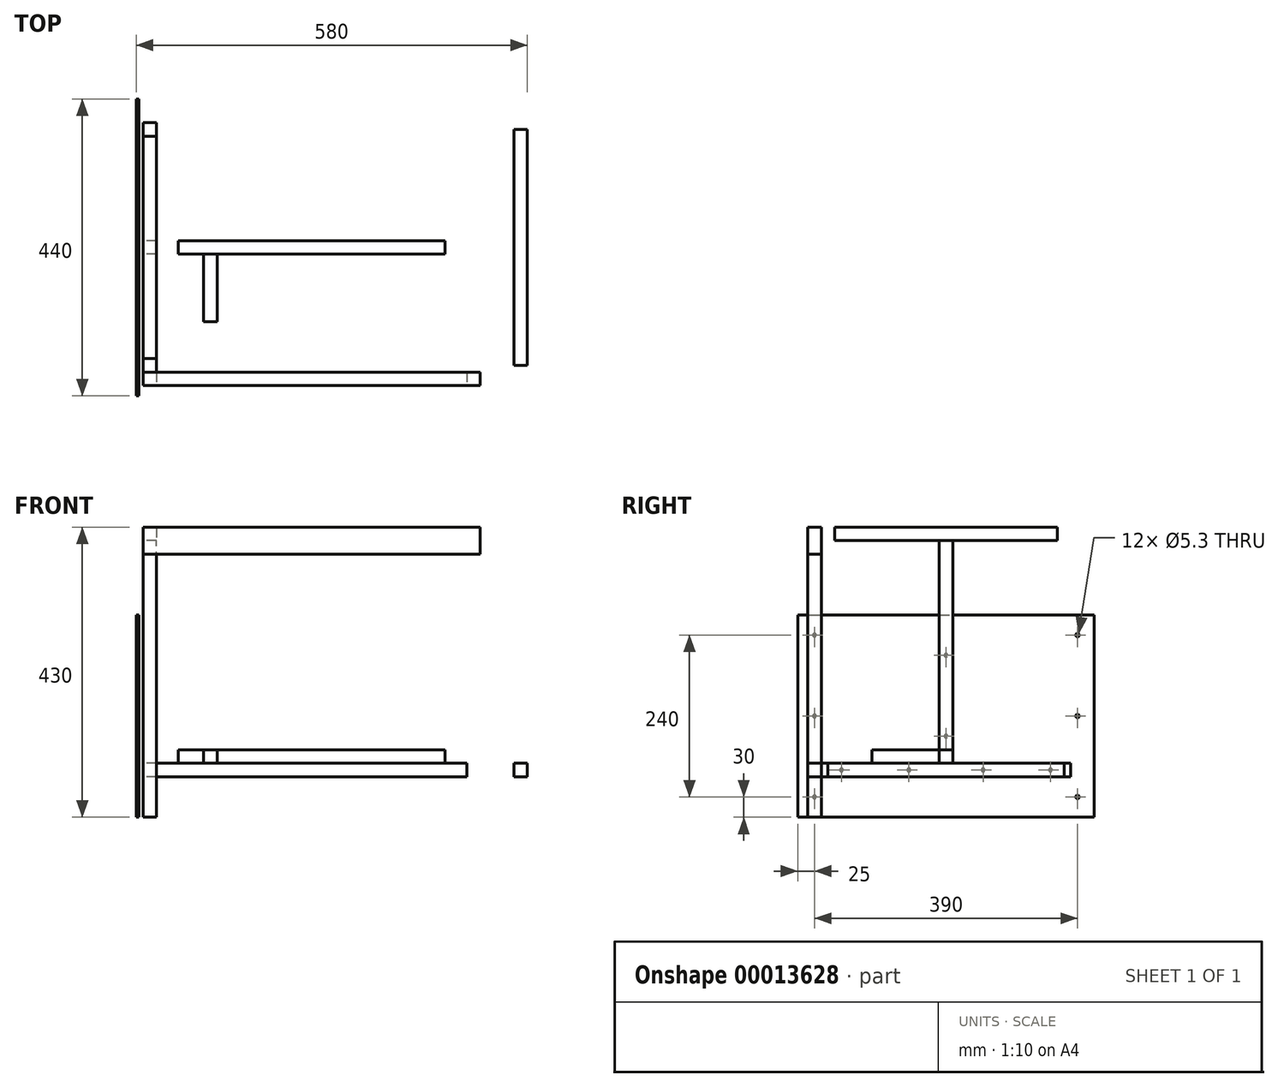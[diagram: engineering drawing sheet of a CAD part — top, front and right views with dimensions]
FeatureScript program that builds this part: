
annotation { "Feature Type Name" : "Feature", "Feature Type Description" : "" }
export const myFeature = defineFeature(function(context is Context, id is Id, definition is map)
    precondition{}
    {
        {
            var Q0;
            Q0=qCreatedBy(makeId("Top.planeOp"),FACE);
            var sketch = newSketch(context, id + "F0", { "sketchPlane" : qUnion([Q0])});
            skLineSegment(sketch, "E0.rect.bottom", {"start": v(230, 185) * mm, "end": v(-230, 185) * mm});
            skLineSegment(sketch, "E0.rect.top", {"start": v(230, -185) * mm, "end": v(-230, -185) * mm});
            skLineSegment(sketch, "E0.rect.left", {"start": v(230, 185) * mm, "end": v(230, -185) * mm});
            skLineSegment(sketch, "E0.rect.right", {"start": v(-230, 185) * mm, "end": v(-230, -185) * mm});
            skPoint(sketch, "E0.rect.middle", {"position": v(0, 0) * mm});
            skLineSegment(sketch, "E1.0", {"start": v(-250, 205) * mm, "end": v(-250, -205) * mm});
            skLineSegment(sketch, "E1.1", {"start": v(250, 205) * mm, "end": v(-250, 205) * mm});
            skLineSegment(sketch, "E1.2", {"start": v(250, 205) * mm, "end": v(250, -205) * mm});
            skLineSegment(sketch, "E1.3", {"start": v(250, -205) * mm, "end": v(-250, -205) * mm});
            skLineSegment(sketch, "E2", {"start": v(230, -185) * mm, "end": v(250, -185) * mm});
            skLineSegment(sketch, "E3", {"start": v(230, -185) * mm, "end": v(230, -205) * mm});
            skLineSegment(sketch, "E4", {"start": v(-230, -185) * mm, "end": v(-230, -205) * mm});
            skLineSegment(sketch, "E5", {"start": v(-230, -185) * mm, "end": v(-250, -185) * mm});
            skLineSegment(sketch, "E6", {"start": v(-230, 185) * mm, "end": v(-250, 185) * mm});
            skLineSegment(sketch, "E7", {"start": v(-230, 185) * mm, "end": v(-230, 205) * mm});
            skLineSegment(sketch, "E8", {"start": v(230, 185) * mm, "end": v(230, 205) * mm});
            skLineSegment(sketch, "E9", {"start": v(230, 185) * mm, "end": v(250, 185) * mm});
            skLineSegment(sketch, "E10.rect.bottom", {"start": v(198, 10) * mm, "end": v(-198, 10) * mm});
            skLineSegment(sketch, "E10.rect.top", {"start": v(198, -10) * mm, "end": v(-198, -10) * mm});
            skLineSegment(sketch, "E10.rect.left", {"start": v(198, 10) * mm, "end": v(198, -10) * mm});
            skLineSegment(sketch, "E10.rect.right", {"start": v(-198, 10) * mm, "end": v(-198, -10) * mm});
            skLineSegment(sketch, "E11", {"start": v(-160, 10) * mm, "end": v(-160, 110) * mm});
            skLineSegment(sketch, "E12", {"start": v(-160, 110) * mm, "end": v(-140, 110) * mm});
            skLineSegment(sketch, "E13", {"start": v(-140, 110) * mm, "end": v(-140, 10) * mm});
            skLineSegment(sketch, "E14", {"start": v(-140, -10) * mm, "end": v(-140, -110) * mm});
            skLineSegment(sketch, "E15", {"start": v(-140, -110) * mm, "end": v(-160, -110) * mm});
            skLineSegment(sketch, "E16", {"start": v(-160, -110) * mm, "end": v(-160, -10) * mm});
            skLineSegment(sketch, "E17", {"start": v(160, 10) * mm, "end": v(160, 110) * mm});
            skLineSegment(sketch, "E18", {"start": v(160, 110) * mm, "end": v(140, 110) * mm});
            skLineSegment(sketch, "E19", {"start": v(140, 110) * mm, "end": v(140, 10) * mm});
            skLineSegment(sketch, "E20", {"start": v(140, -10) * mm, "end": v(140, -110) * mm});
            skLineSegment(sketch, "E21", {"start": v(140, -110) * mm, "end": v(160, -110) * mm});
            skLineSegment(sketch, "E22", {"start": v(160, -110) * mm, "end": v(160, -10) * mm});
            skLineSegment(sketch, "E23", {"start": v(0, 0) * mm, "end": v(140, 0) * mm, "construction": true});
            skLineSegment(sketch, "E24", {"start": v(0, 0) * mm, "end": v(-140, 0) * mm, "construction": true});
            skLineSegment(sketch, "E25.rect.bottom", {"start": v(-184, 1) * mm, "end": v(-226, 1) * mm, "construction": true});
            skLineSegment(sketch, "E25.rect.top", {"start": v(-184, -41) * mm, "end": v(-226, -41) * mm, "construction": true});
            skLineSegment(sketch, "E25.rect.left", {"start": v(-184, 1) * mm, "end": v(-184, -41) * mm, "construction": true});
            skLineSegment(sketch, "E25.rect.right", {"start": v(-226, 1) * mm, "end": v(-226, -41) * mm, "construction": true});
            skPoint(sketch, "E25.rect.middle", {"position": v(-205, -20) * mm});
            skCircle(sketch, "E26", {"center": v(-205, -20) * mm, "radius": 12.5 * mm, "construction": true});
            skLineSegment(sketch, "E27", {"start": v(0, 0) * mm, "end": v(0, 205) * mm, "construction": true});
            skCircle(sketch, "E28.0.MirrorC", {"center": v(205, -20) * mm, "radius": 12.5 * mm, "construction": true});
            skLineSegment(sketch, "E29.0.MirrorCS", {"start": v(184, 1) * mm, "end": v(184, -41) * mm, "construction": true});
            skLineSegment(sketch, "E30.0.MirrorCS", {"start": v(184, 1) * mm, "end": v(226, 1) * mm, "construction": true});
            skLineSegment(sketch, "E31.0.MirrorCS", {"start": v(226, 1) * mm, "end": v(226, -41) * mm, "construction": true});
            skLineSegment(sketch, "E32.0.MirrorCS", {"start": v(184, -41) * mm, "end": v(226, -41) * mm, "construction": true});
            skLineSegment(sketch, "E33", {"start": v(-230, -10) * mm, "end": v(-250, -10) * mm});
            skLineSegment(sketch, "E34", {"start": v(-230, 10) * mm, "end": v(-250, 10) * mm});
            skLineSegment(sketch, "E35", {"start": v(230, 10) * mm, "end": v(250, 10) * mm});
            skLineSegment(sketch, "E36", {"start": v(230, -10) * mm, "end": v(250, -10) * mm});
            skLineSegment(sketch, "E37.rect.bottom", {"start": v(320, 175) * mm, "end": v(300, 175) * mm});
            skLineSegment(sketch, "E37.rect.top", {"start": v(320, -175) * mm, "end": v(300, -175) * mm});
            skLineSegment(sketch, "E37.rect.left", {"start": v(320, 175) * mm, "end": v(320, -175) * mm});
            skLineSegment(sketch, "E37.rect.right", {"start": v(300, 175) * mm, "end": v(300, -175) * mm});
            skPoint(sketch, "E37.rect.middle", {"position": v(310, 0) * mm});
            skCircle(sketch, "E38", {"center": v(-205, -20) * mm, "radius": 5.5 * mm, "construction": true});
            skSolve(sketch);
        }
        {
            var Q0;
            Q0=sQuery(id+"F0.wireOp",EDGE,"E1.3");
            cPlane(context, id + "F1", {"entities" : qUnion([Q0]), "cplaneType" : CPlaneType.LINE_ANGLE, "offset" : 150 * mm, "angle" : 0 * degree, "width" : 150 * mm, "height" : 150 * mm});
        }
        {
            var Q0;
            Q0=qCreatedBy(id+"F1.planeOp",FACE);
            var sketch = newSketch(context, id + "F2", { "sketchPlane" : qUnion([Q0])});
            skLineSegment(sketch, "E39.0", {"start": v(250, 0) * mm, "end": v(-230, 0) * mm});
            skLineSegment(sketch, "E40", {"start": v(-250, 0) * mm, "end": v(-250, 310) * mm});
            skLineSegment(sketch, "E41", {"start": v(-250, 310) * mm, "end": v(250, 310) * mm});
            skLineSegment(sketch, "E42", {"start": v(250, 310) * mm, "end": v(250, 0) * mm});
            skLineSegment(sketch, "E43", {"start": v(-250, 310) * mm, "end": v(-250, 350) * mm});
            skLineSegment(sketch, "E44", {"start": v(-250, 350) * mm, "end": v(250, 350) * mm});
            skLineSegment(sketch, "E45", {"start": v(250, 350) * mm, "end": v(250, 310) * mm});
            skLineSegment(sketch, "E46", {"start": v(-250, 0) * mm, "end": v(-250, -20) * mm});
            skLineSegment(sketch, "E47", {"start": v(-250, -20) * mm, "end": v(250, -20) * mm});
            skLineSegment(sketch, "E48", {"start": v(250, -20) * mm, "end": v(250, 0) * mm});
            skPoint(sketch, "E49.0", {"position": v(-230, 0) * mm});
            skPoint(sketch, "E50.0", {"position": v(230, 0) * mm});
            skLineSegment(sketch, "E51", {"start": v(230, 0) * mm, "end": v(230, -20) * mm});
            skLineSegment(sketch, "E52", {"start": v(-230, 0) * mm, "end": v(-230, -20) * mm});
            skLineSegment(sketch, "E53", {"start": v(-230, 0) * mm, "end": v(-230, 310) * mm});
            skLineSegment(sketch, "E54", {"start": v(230, 0) * mm, "end": v(230, 310) * mm});
            skLineSegment(sketch, "E55", {"start": v(-230, -20) * mm, "end": v(-230, -80) * mm});
            skLineSegment(sketch, "E56", {"start": v(-230, -80) * mm, "end": v(-250, -80) * mm});
            skLineSegment(sketch, "E57", {"start": v(-250, -80) * mm, "end": v(-250, -20) * mm});
            skSolve(sketch);
        }
        {
            var Q0;
            Q0=sQuery(id+"F0.wireOp",EDGE,"E1.0");
            cPlane(context, id + "F3", {"entities" : qUnion([Q0]), "cplaneType" : CPlaneType.LINE_ANGLE, "offset" : 150 * mm, "angle" : 90 * degree, "width" : 150 * mm, "height" : 150 * mm});
        }
        {
            var Q0;
            Q0=qCreatedBy(id+"F3.planeOp",FACE);
            var sketch = newSketch(context, id + "F4", { "sketchPlane" : qUnion([Q0])});
            skLineSegment(sketch, "E58.0", {"start": v(185, 0) * mm, "end": v(-185, 0) * mm});
            skPoint(sketch, "E59.1", {"position": v(-185, 0) * mm});
            skPoint(sketch, "E60.0", {"position": v(-205, 310) * mm});
            skPoint(sketch, "E60.1", {"position": v(-205, 350) * mm});
            skPoint(sketch, "E61.0", {"position": v(185, 0) * mm});
            skPoint(sketch, "E62.0", {"position": v(10, 0) * mm});
            skPoint(sketch, "E63.0", {"position": v(-10, 0) * mm});
            skPoint(sketch, "E64.0", {"position": v(-205, -20) * mm});
            skLineSegment(sketch, "E65", {"start": v(-205, -20) * mm, "end": v(205, -20) * mm});
            skLineSegment(sketch, "E66", {"start": v(205, -20) * mm, "end": v(205, 0) * mm});
            skLineSegment(sketch, "E67", {"start": v(-205, 350) * mm, "end": v(-185, 350) * mm});
            skLineSegment(sketch, "E68", {"start": v(-185, 350) * mm, "end": v(-185, 310) * mm});
            skLineSegment(sketch, "E69", {"start": v(-167.1, 310) * mm, "end": v(-185, 310) * mm});
            skLineSegment(sketch, "E70", {"start": v(-205, 350) * mm, "end": v(-205, 310) * mm});
            skLineSegment(sketch, "E71", {"start": v(-185, 350) * mm, "end": v(185, 350) * mm});
            skLineSegment(sketch, "E72", {"start": v(185, 350) * mm, "end": v(185, 330) * mm});
            skLineSegment(sketch, "E73", {"start": v(185, 330) * mm, "end": v(-185, 330) * mm});
            skLineSegment(sketch, "E74", {"start": v(185, 350) * mm, "end": v(205, 350) * mm});
            skLineSegment(sketch, "E75", {"start": v(205, 350) * mm, "end": v(205, 310) * mm});
            skLineSegment(sketch, "E76", {"start": v(205, 310) * mm, "end": v(185, 310) * mm});
            skLineSegment(sketch, "E77", {"start": v(185, 310) * mm, "end": v(185, 330) * mm});
            skLineSegment(sketch, "E78", {"start": v(205, 0) * mm, "end": v(205, 310) * mm});
            skLineSegment(sketch, "E79", {"start": v(185, 310) * mm, "end": v(185, 0) * mm});
            skLineSegment(sketch, "E80", {"start": v(-185, 310) * mm, "end": v(-185, 0) * mm});
            skLineSegment(sketch, "E81", {"start": v(-205, 0) * mm, "end": v(-205, 310) * mm});
            skLineSegment(sketch, "E82", {"start": v(-205, -20) * mm, "end": v(-205, 0) * mm});
            skLineSegment(sketch, "E83", {"start": v(-10, 0) * mm, "end": v(-10, 330) * mm});
            skLineSegment(sketch, "E84", {"start": v(10, 0) * mm, "end": v(10, 330) * mm});
            skLineSegment(sketch, "E85", {"start": v(-185, 0) * mm, "end": v(-185, -20) * mm});
            skLineSegment(sketch, "E86", {"start": v(185, 0) * mm, "end": v(185, -20) * mm});
            skLineSegment(sketch, "E87", {"start": v(-165, 350) * mm, "end": v(-165, 330) * mm});
            skLineSegment(sketch, "E88", {"start": v(-165, 340) * mm, "end": v(-185, 340) * mm, "construction": true});
            skLineSegment(sketch, "E89", {"start": v(165, 350) * mm, "end": v(165, 330) * mm});
            skLineSegment(sketch, "E90", {"start": v(165, 340) * mm, "end": v(185, 340) * mm, "construction": true});
            skSolve(sketch);
        }
        {
            var Q0;
            {var subQ1=sQuery(id+"F2.wireOp",EDGE,"E51");Q0=makeQuery(id+"F2.imprint","IMPRINT",FACE,{"disambiguationData":[TD([[makeQuery(id+"F2.imprint","IMPRINT",EDGE,{"derivedFrom":subQ1}),-1.0]])]});}
            extrude(context, id + "F5", {"entities" : qUnion([Q0]), "oppositeDirection" : true, "depth" : 20 * mm});
        }
        {
            var Q0;
            {var subQ1=sQuery(id+"F4.wireOp",EDGE,"E85");Q0=makeQuery(id+"F4.imprint","IMPRINT",FACE,{"disambiguationData":[TD([[makeQuery(id+"F4.imprint","IMPRINT",EDGE,{"derivedFrom":subQ1}),1.0]])]});}
            extrude(context, id + "F6", {"entities" : qUnion([Q0]), "depth" : 20 * mm});
        }
        {
            var Q0;
            {var subQ3=sQuery(id+"F2.wireOp",EDGE,"E40");Q0=makeQuery(id+"F2.imprint","IMPRINT",FACE,{"disambiguationData":[TD([[makeQuery(id+"F2.imprint","IMPRINT",EDGE,{"derivedFrom":subQ3}),-1.0]])]});}
            var Q1;
            {var subQ1=sQuery(id+"F2.wireOp",EDGE,"E55");Q1=makeQuery(id+"F2.imprint","IMPRINT",FACE,{"disambiguationData":[TD([[makeQuery(id+"F2.imprint","IMPRINT",EDGE,{"derivedFrom":subQ1}),-1.0]])]});}
            extrude(context, id + "F7", {"entities" : qUnion([Q0, Q1]), "oppositeDirection" : true, "depth" : 20 * mm});
        }
        {
            var Q0;
            {var subQ1=sQuery(id+"F4.wireOp",EDGE,"E87");Q0=makeQuery(id+"F4.imprint","IMPRINT",FACE,{"disambiguationData":[TD([[makeQuery(id+"F4.imprint","IMPRINT",EDGE,{"derivedFrom":subQ1}),1.0]])]});}
            extrude(context, id + "F8", {"entities" : qUnion([Q0]), "depth" : 20 * mm});
        }
        {
            var Q0;
            {var subQ1=sQuery(id+"F2.wireOp",EDGE,"E43");Q0=makeQuery(id+"F2.imprint","IMPRINT",FACE,{"disambiguationData":[TD([[makeQuery(id+"F2.imprint","IMPRINT",EDGE,{"derivedFrom":subQ1}),-1.0]])]});}
            extrude(context, id + "F9", {"entities" : qUnion([Q0]), "oppositeDirection" : true, "depth" : 20 * mm});
        }
        {
            var Q0;
            Q0=makeQuery(id+"F0.imprint","IMPRINT",FACE,{"disambiguationData":[TD([[makeQuery(id+"F0.imprint","IMPRINT",EDGE,{"derivedFrom":sQuery(id+"F0.wireOp",EDGE,"E37.rect.bottom")}),1.0]])]});
            extrude(context, id + "F10", {"entities" : qUnion([Q0]), "oppositeDirection" : true, "depth" : 20 * mm});
        }
        {
            var Q0;
            {var subQ1=sQuery(id+"F4.wireOp",EDGE,"E83");Q0=makeQuery(id+"F4.imprint","IMPRINT",FACE,{"disambiguationData":[TD([[makeQuery(id+"F4.imprint","IMPRINT",EDGE,{"derivedFrom":subQ1}),-1.0]])]});}
            extrude(context, id + "F11", {"entities" : qUnion([Q0]), "depth" : 20 * mm});
        }
        {
            var Q0;
            {var subQ6=sQuery(id+"F0.wireOp",EDGE,"E10.rect.left");Q0=makeQuery(id+"F0.imprint","IMPRINT",FACE,{"disambiguationData":[TD([[makeQuery(id+"F0.imprint","IMPRINT",EDGE,{"derivedFrom":subQ6}),-1.0]])]});}
            extrude(context, id + "F12", {"entities" : qUnion([Q0]), "depth" : 20 * mm});
        }
        {
            var Q0;
            {var subQ1=sQuery(id+"F0.wireOp",EDGE,"E14");Q0=makeQuery(id+"F0.imprint","IMPRINT",FACE,{"disambiguationData":[TD([[makeQuery(id+"F0.imprint","IMPRINT",EDGE,{"derivedFrom":subQ1}),-1.0]])]});}
            extrude(context, id + "F13", {"entities" : qUnion([Q0]), "depth" : 20 * mm});
        }
        {
            var Q0;
            {var subQ1=sQuery(id+"F4.wireOp",EDGE,"E85");Q0=makeQuery(id+"F4.imprint","IMPRINT",FACE,{"disambiguationData":[TD([[makeQuery(id+"F4.imprint","IMPRINT",EDGE,{"derivedFrom":subQ1}),1.0]])]});}
            cPlane(context, id + "F14", {"entities" : qUnion([Q0]), "cplaneType" : CPlaneType.OFFSET, "offset" : 10 * mm, "oppositeDirection" : true, "width" : 150 * mm, "height" : 150 * mm});
        }
        {
            var Q0;
            Q0=qCreatedBy(id+"F14.planeOp",FACE);
            var sketch = newSketch(context, id + "F15", { "sketchPlane" : qUnion([Q0])});
            skLineSegment(sketch, "E91.0", {"start": v(-185, 310) * mm, "end": v(-205, 310) * mm, "construction": true});
            skLineSegment(sketch, "E92.0", {"start": v(-185, 350) * mm, "end": v(-205, 350) * mm, "construction": true});
            skLineSegment(sketch, "E93.0", {"start": v(-185, -80) * mm, "end": v(-205, -80) * mm, "construction": true});
            skLineSegment(sketch, "E94.0", {"start": v(165, 350) * mm, "end": v(165, 330) * mm, "construction": true});
            skLineSegment(sketch, "E95.0", {"start": v(-165, 350) * mm, "end": v(-165, 330) * mm, "construction": true});
            skLineSegment(sketch, "E96.0", {"start": v(-185, -20) * mm, "end": v(185, -20) * mm, "construction": true});
            skLineSegment(sketch, "E97.0", {"start": v(185, 0) * mm, "end": v(-185, 0) * mm, "construction": true});
            skLineSegment(sketch, "E98.0", {"start": v(10, 0) * mm, "end": v(10, 330) * mm, "construction": true});
            skLineSegment(sketch, "E99.0", {"start": v(-10, 0) * mm, "end": v(-10, 330) * mm, "construction": true});
            skLineSegment(sketch, "E100.rect.bottom", {"start": v(-220, -80) * mm, "end": v(220, -80) * mm});
            skLineSegment(sketch, "E100.rect.top", {"start": v(-220, 220) * mm, "end": v(220, 220) * mm});
            skLineSegment(sketch, "E100.rect.left", {"start": v(-220, -80) * mm, "end": v(-220, 220) * mm});
            skLineSegment(sketch, "E100.rect.right", {"start": v(220, -80) * mm, "end": v(220, 220) * mm});
            skPoint(sketch, "E100.rect.middle", {"position": v(0, 70) * mm});
            skLineSegment(sketch, "E101", {"start": v(0, 70) * mm, "end": v(0, 220) * mm, "construction": true});
            skLineSegment(sketch, "E102.0.MirrorCS", {"start": v(185, 350) * mm, "end": v(205, 350) * mm, "construction": true});
            skLineSegment(sketch, "E103.0.MirrorCS", {"start": v(185, 310) * mm, "end": v(205, 310) * mm, "construction": true});
            skLineSegment(sketch, "E104.0.MirrorCS", {"start": v(185, -80) * mm, "end": v(205, -80) * mm, "construction": true});
            skLineSegment(sketch, "E105", {"start": v(205, -80) * mm, "end": v(205, 350) * mm, "construction": true});
            skLineSegment(sketch, "E106", {"start": v(-205, 350) * mm, "end": v(-205, -80) * mm, "construction": true});
            skLineSegment(sketch, "E107", {"start": v(185, 350) * mm, "end": v(185, -80) * mm, "construction": true});
            skLineSegment(sketch, "E108", {"start": v(-185, 350) * mm, "end": v(-185, -80) * mm, "construction": true});
            skCircle(sketch, "E109", {"center": v(-155, -10) * mm, "radius": 2.65 * mm});
            skCircle(sketch, "E110", {"center": v(-55, -10) * mm, "radius": 2.65 * mm});
            skCircle(sketch, "E111", {"center": v(-195, -50) * mm, "radius": 2.65 * mm});
            skCircle(sketch, "E112.0.1.0", {"center": v(-195, 70) * mm, "radius": 2.65 * mm});
            skCircle(sketch, "E112.0.2.0", {"center": v(-195, 190) * mm, "radius": 2.65 * mm});
            skLineSegment(sketch, "E112.direction1", {"start": v(-195, -50) * mm, "end": v(-170, -50) * mm, "construction": true});
            skLineSegment(sketch, "E112.direction2", {"start": v(-195, -50) * mm, "end": v(-195, 70) * mm, "construction": true});
            skCircle(sketch, "E113", {"center": v(0, 40) * mm, "radius": 2.65 * mm});
            skCircle(sketch, "E114.0.1.0", {"center": v(0, 160) * mm, "radius": 2.65 * mm});
            skLineSegment(sketch, "E114.direction1", {"start": v(0, 40) * mm, "end": v(25, 40) * mm, "construction": true});
            skLineSegment(sketch, "E114.direction2", {"start": v(0, 40) * mm, "end": v(0, 160) * mm, "construction": true});
            skCircle(sketch, "E115.0.MirrorC", {"center": v(195, 190) * mm, "radius": 2.65 * mm});
            skCircle(sketch, "E116.0.MirrorC", {"center": v(195, 70) * mm, "radius": 2.65 * mm});
            skCircle(sketch, "E117.0.MirrorC", {"center": v(195, -50) * mm, "radius": 2.65 * mm});
            skCircle(sketch, "E118.0.MirrorC", {"center": v(155, -10) * mm, "radius": 2.65 * mm});
            skCircle(sketch, "E119.0.MirrorC", {"center": v(55, -10) * mm, "radius": 2.65 * mm});
            skSolve(sketch);
        }
        {
            var Q0;
            Q0=makeQuery(id+"F15.imprint","IMPRINT",FACE,{"disambiguationData":[TD([[makeQuery(id+"F15.imprint","IMPRINT",EDGE,{"derivedFrom":sQuery(id+"F15.wireOp",EDGE,"E100.rect.bottom")}),1.0]])]});
            extrude(context, id + "F16", {"entities" : qUnion([Q0]), "depth" : 3.6 * mm});
        }
    });
